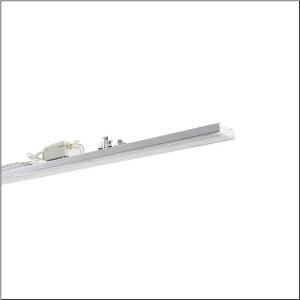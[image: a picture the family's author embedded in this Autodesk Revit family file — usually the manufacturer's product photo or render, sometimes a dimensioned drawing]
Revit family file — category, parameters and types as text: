
# Revit family: licross_r__21_recessed_mo_52tl1ede445g_0dac
name_source: partatom
category: Lighting Fixtures
units: mm (PartAtom-declared; Revit-internal decimal feet)

## family parameters
Cut with Voids When Loaded = No
Host = Face
Light Source = No
Part Type = Normal
Room Calculation Point = No
Round Connector Dimension = Use Diameter
Shared = No

## types (1)
- --- (1 x LED, 4970 lm, 29.9 W, 4000K)
    Apparent Load = 30 VA
    CIE Flux Codes = 85 95 99 100 100
    Color Rendering = 80
    Color Temperature = 4000K
    Default Elevation = 1800 mm
    Description = Licross® 21 Recessed MO, luminaire insert, of sheet steel, galvanised, coil coated, white, length: 750mm, width: 66mm, height: 67mm, LED rated luminous flux: 4.970lm, light colour: 840, control gear: DALI 2, with plug, 5-pole, with phase selection, mains connection: 220..240V, AC, 50/60Hz, rated input power: 30W, halogen-free wiring, primary light control with lens, of plastic, primary optical cover: cover, of PMMA, light emission: direct distribution, primary light characteristic: symmetric, protection rating (complete): IP40, insulation class (complete): insulation class I (protective earthing), certification: CE, ENEC, VDE, UKCA, protection symbol: D if used in an environment without relevant dust loads with corresponding accessories, impact resistance: IK06, permissible ambient temperature for indoor applications: -25..+35°C, corresponds to IFS (International Featured Standards) requirements for safety and quality in the food industry, reducing of maximum allowable ambient temperature of 5°C with ceiling mounting, LABS conformity tested according to VDMA 24364:2018-05, packaging unit: 1 piece
    Height = 58 mm
    Lamp = 1 x LED
    Lamp Light Flux = 4970 lm
    Lamp Power = 29.9 W
    Lamp count = 1
    Length = 750 mm
    Luminous efficacy = 166 lm/W
    Manufacturer = Siteco
    ModVariant = No
    Model = 52TL1EDE445G
    Mounting Place = Ceiling
    Mounting Type = Pendant
    Number of Poles = 1
    OnlyDefault = Yes
    Power Factor = 1
    Product Name = Licross® 21 Recessed MO
    Product group = luminaire insert
    ProductGroupID = 901
    Protection Class = Protection class I
    Protection Degree = IP 40
    RLX_Detail_Level = 1
    RLX_Emergency_Light_Flux = 0 lm
    RLX_Emergency_Type = 0
    RLX_Emergency_Type_DB = No
    RlxData = <blob elided: 28941 chars, md5=d706a849>
    Socket = socket
    Standby Power = 0 W
    System Light Flux = 4970 lm
    System Power = 30 W
    Type Comments = factory setting: luminous flux: 100 % | dim-lin: 254 | 390 mA
    Type Image = l_1296930.jpg
    URL = http://relux.com
    VarID = @adj_057209
    Voltage = 0 V
    Weight = 0.00 kg
    Width = 66 mm

## geometry (parser evidence)
native form markers: Blend x4, Sweep x8
no freeform markers — native parametric forms only
